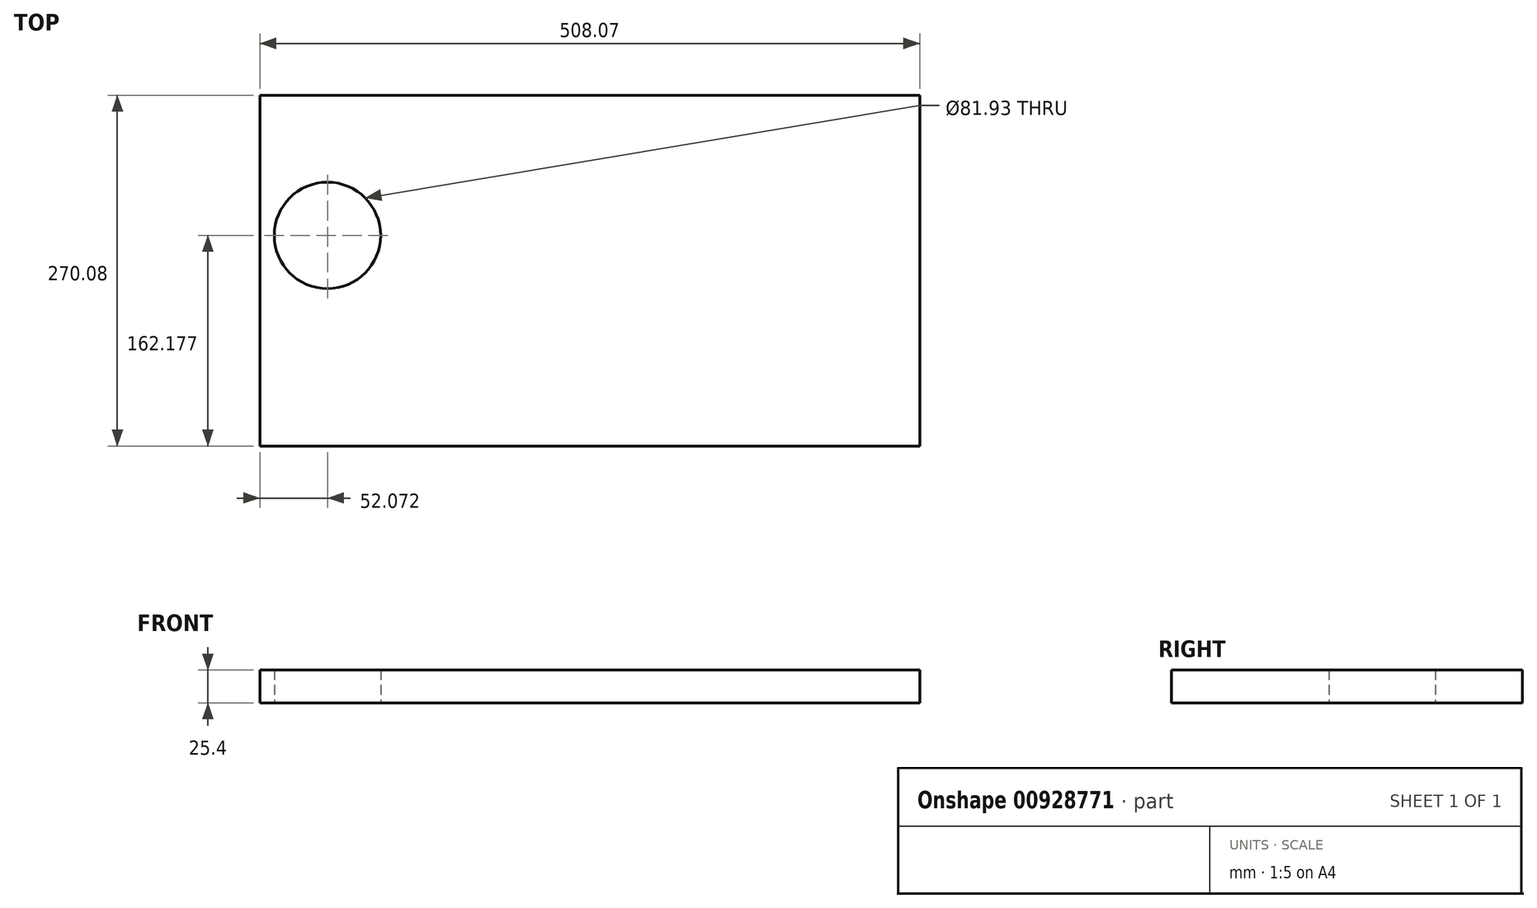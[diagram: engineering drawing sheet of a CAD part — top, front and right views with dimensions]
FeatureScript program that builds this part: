
annotation { "Feature Type Name" : "Feature", "Feature Type Description" : "" }
export const myFeature = defineFeature(function(context is Context, id is Id, definition is map)
    precondition{}
    {
        {
            var Q0;
            Q0=qCreatedBy(makeId("Top.planeOp"),FACE);
            var sketch = newSketch(context, id + "F0", { "sketchPlane" : qUnion([Q0])});
            skLineSegment(sketch, "E0.bottom", {"start": v(-240.89, 123.22) * mm, "end": v(267.18, 123.22) * mm});
            skLineSegment(sketch, "E0.top", {"start": v(-240.89, -146.86) * mm, "end": v(267.18, -146.86) * mm});
            skLineSegment(sketch, "E0.left", {"start": v(-240.89, 123.22) * mm, "end": v(-240.89, -146.86) * mm});
            skLineSegment(sketch, "E0.right", {"start": v(267.18, 123.22) * mm, "end": v(267.18, -146.86) * mm});
            skCircle(sketch, "E1", {"center": v(-188.82, 15.32) * mm, "radius": 40.96 * mm});
            skSolve(sketch);
        }
        {
            var Q0;
            Q0=makeQuery(id+"F0.imprint","IMPRINT",FACE,{"disambiguationData":[TD([[makeQuery(id+"F0.imprint","IMPRINT",EDGE,{"derivedFrom":sQuery(id+"F0.wireOp",EDGE,"E0.bottom")}),-1.0]])]});
            extrude(context, id + "F1", {"entities" : qUnion([Q0]), "depth" : 25.4 * mm, "offsetDistance" : 25.4 * mm});
        }
    });
